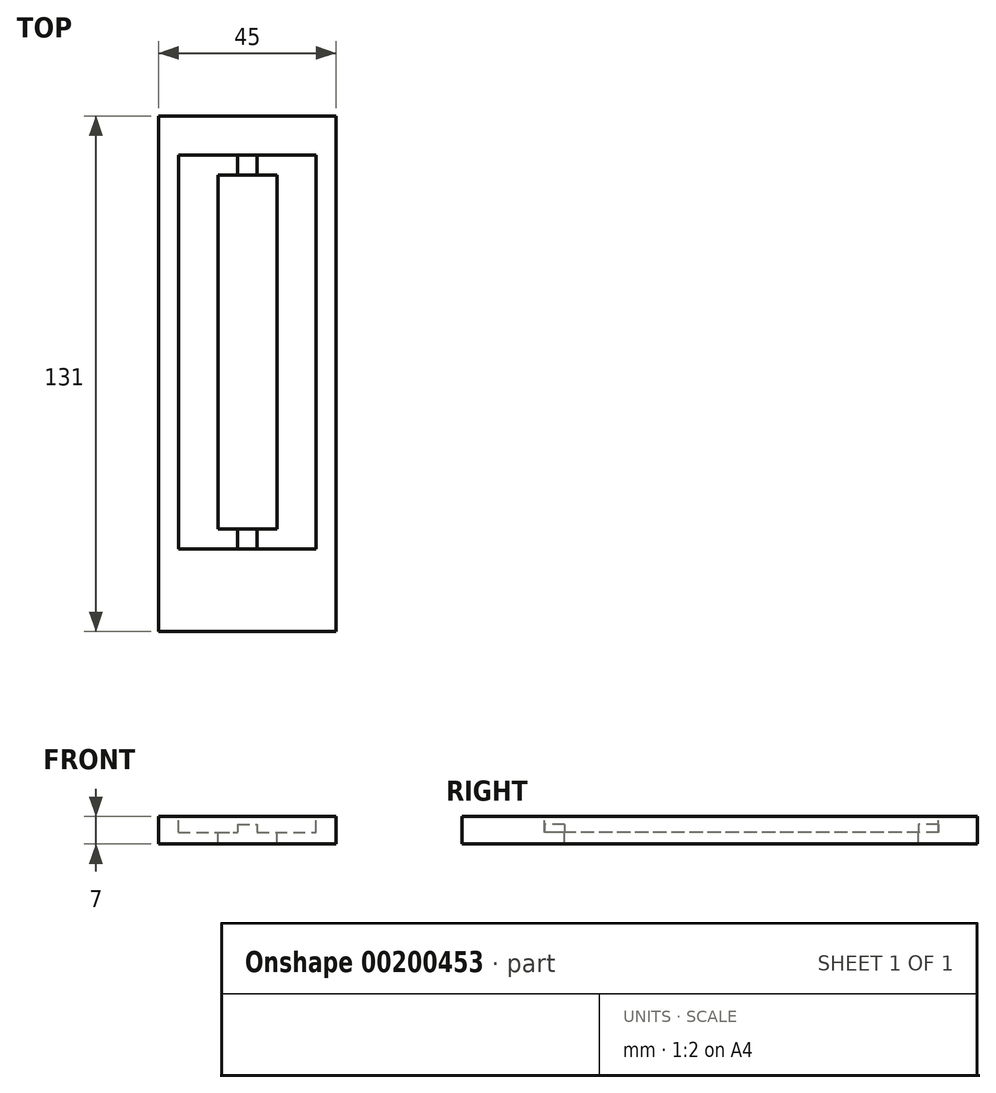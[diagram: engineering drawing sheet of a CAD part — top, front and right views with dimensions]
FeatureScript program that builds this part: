
annotation { "Feature Type Name" : "Feature", "Feature Type Description" : "" }
export const myFeature = defineFeature(function(context is Context, id is Id, definition is map)
    precondition{}
    {
        {
            var Q0;
            Q0=qCreatedBy(makeId("Top.planeOp"),FACE);
            var sketch = newSketch(context, id + "F0", { "sketchPlane" : qUnion([Q0])});
            skLineSegment(sketch, "E0.bottom", {"start": v(0, 0) * mm, "end": v(45, 0) * mm});
            skLineSegment(sketch, "E0.top", {"start": v(0, 131) * mm, "end": v(45, 131) * mm});
            skLineSegment(sketch, "E0.left", {"start": v(0, 0) * mm, "end": v(0, 131) * mm});
            skLineSegment(sketch, "E0.right", {"start": v(45, 0) * mm, "end": v(45, 131) * mm});
            skSolve(sketch);
        }
        {
            var Q0;
            Q0=qSketchRegion(id+"F0",true);
            extrude(context, id + "F1", {"entities" : qUnion([Q0]), "depth" : 2 * mm});
        }
        {
            var Q0;
            Q0=makeQuery(id+"F1.opExtrude","CAP_FACE",FACE,{"disambiguationData":[OSD([sQuery(id+"F0.wireOp",EDGE,"E0.bottom"),sQuery(id+"F0.wireOp",EDGE,"E0.top"),sQuery(id+"F0.wireOp",EDGE,"E0.left"),sQuery(id+"F0.wireOp",EDGE,"E0.right")])],"isStart":false});
            var sketch = newSketch(context, id + "F2", { "sketchPlane" : qUnion([Q0])});
            skLineSegment(sketch, "E1.bottom", {"start": v(0, 0) * mm, "end": v(45, 0) * mm});
            skLineSegment(sketch, "E1.top", {"start": v(0, 131) * mm, "end": v(45, 131) * mm});
            skLineSegment(sketch, "E1.left", {"start": v(0, 0) * mm, "end": v(0, 131) * mm});
            skLineSegment(sketch, "E1.right", {"start": v(45, 0) * mm, "end": v(45, 131) * mm});
            skSolve(sketch);
        }
        {
            var Q0;
            Q0=qSketchRegion(id+"F2",true);
            extrude(context, id + "F3", {"entities" : qUnion([Q0]), "operationType" : NewBodyOperationType.ADD, "depth" : 5 * mm});
        }
        {
            var Q0;
            Q0=makeQuery(id+"F3.opExtrude","CAP_FACE",FACE,{"disambiguationData":[OSD([sQuery(id+"F2.wireOp",EDGE,"E1.bottom"),sQuery(id+"F2.wireOp",EDGE,"E1.top"),sQuery(id+"F2.wireOp",EDGE,"E1.left"),sQuery(id+"F2.wireOp",EDGE,"E1.right")])],"isStart":false});
            var sketch = newSketch(context, id + "F4", { "sketchPlane" : qUnion([Q0])});
            skLineSegment(sketch, "E2.bottom", {"start": v(15, 116) * mm, "end": v(30, 116) * mm});
            skLineSegment(sketch, "E2.top", {"start": v(15, 26) * mm, "end": v(30, 26) * mm});
            skLineSegment(sketch, "E2.left", {"start": v(15, 116) * mm, "end": v(15, 26) * mm});
            skLineSegment(sketch, "E2.right", {"start": v(30, 116) * mm, "end": v(30, 26) * mm});
            skSolve(sketch);
        }
        {
            var Q0;
            Q0=makeQuery(id+"F3.opExtrude","CAP_FACE",FACE,{"disambiguationData":[OSD([sQuery(id+"F2.wireOp",EDGE,"E1.bottom"),sQuery(id+"F2.wireOp",EDGE,"E1.top"),sQuery(id+"F2.wireOp",EDGE,"E1.left"),sQuery(id+"F2.wireOp",EDGE,"E1.right")])],"isStart":false});
            var sketch = newSketch(context, id + "F5", { "sketchPlane" : qUnion([Q0])});
            skLineSegment(sketch, "E3.bottom", {"start": v(5, 121) * mm, "end": v(40, 121) * mm});
            skLineSegment(sketch, "E3.top", {"start": v(5, 21) * mm, "end": v(40, 21) * mm});
            skLineSegment(sketch, "E3.left", {"start": v(5, 121) * mm, "end": v(5, 21) * mm});
            skLineSegment(sketch, "E3.right", {"start": v(40, 121) * mm, "end": v(40, 21) * mm});
            skSolve(sketch);
        }
        {
            var Q0;
            Q0=qSketchRegion(id+"F5",true);
            extrude(context, id + "F6", {"entities" : qUnion([Q0]), "operationType" : NewBodyOperationType.REMOVE, "oppositeDirection" : true, "depth" : 4 * mm});
        }
        {
            var Q0;
            Q0=makeQuery(id+"F6.boolean.opBoolean","COPY",FACE,{"derivedFrom":makeQuery(id+"F6.opExtrude","CAP_FACE",FACE,{"disambiguationData":[OSD([sQuery(id+"F5.wireOp",EDGE,"E3.bottom"),sQuery(id+"F5.wireOp",EDGE,"E3.top"),sQuery(id+"F5.wireOp",EDGE,"E3.left"),sQuery(id+"F5.wireOp",EDGE,"E3.right")])],"isStart":false})});
            var sketch = newSketch(context, id + "F7", { "sketchPlane" : qUnion([Q0])});
            skLineSegment(sketch, "E4.bottom", {"start": v(20, 121) * mm, "end": v(25, 121) * mm});
            skLineSegment(sketch, "E4.top", {"start": v(20, 21) * mm, "end": v(25, 21) * mm});
            skLineSegment(sketch, "E4.left", {"start": v(20, 121) * mm, "end": v(20, 21) * mm});
            skLineSegment(sketch, "E4.right", {"start": v(25, 121) * mm, "end": v(25, 21) * mm});
            skSolve(sketch);
        }
        {
            var Q0;
            Q0=qSketchRegion(id+"F7",true);
            extrude(context, id + "F8", {"entities" : qUnion([Q0]), "operationType" : NewBodyOperationType.ADD, "depth" : 2 * mm});
        }
        {
            var Q0;
            Q0=qSketchRegion(id+"F4",true);
            extrude(context, id + "F9", {"entities" : qUnion([Q0]), "operationType" : NewBodyOperationType.REMOVE, "endBound" : BoundingType.THROUGH_ALL, "oppositeDirection" : true, "depth" : 25.4 * mm});
        }
    });
